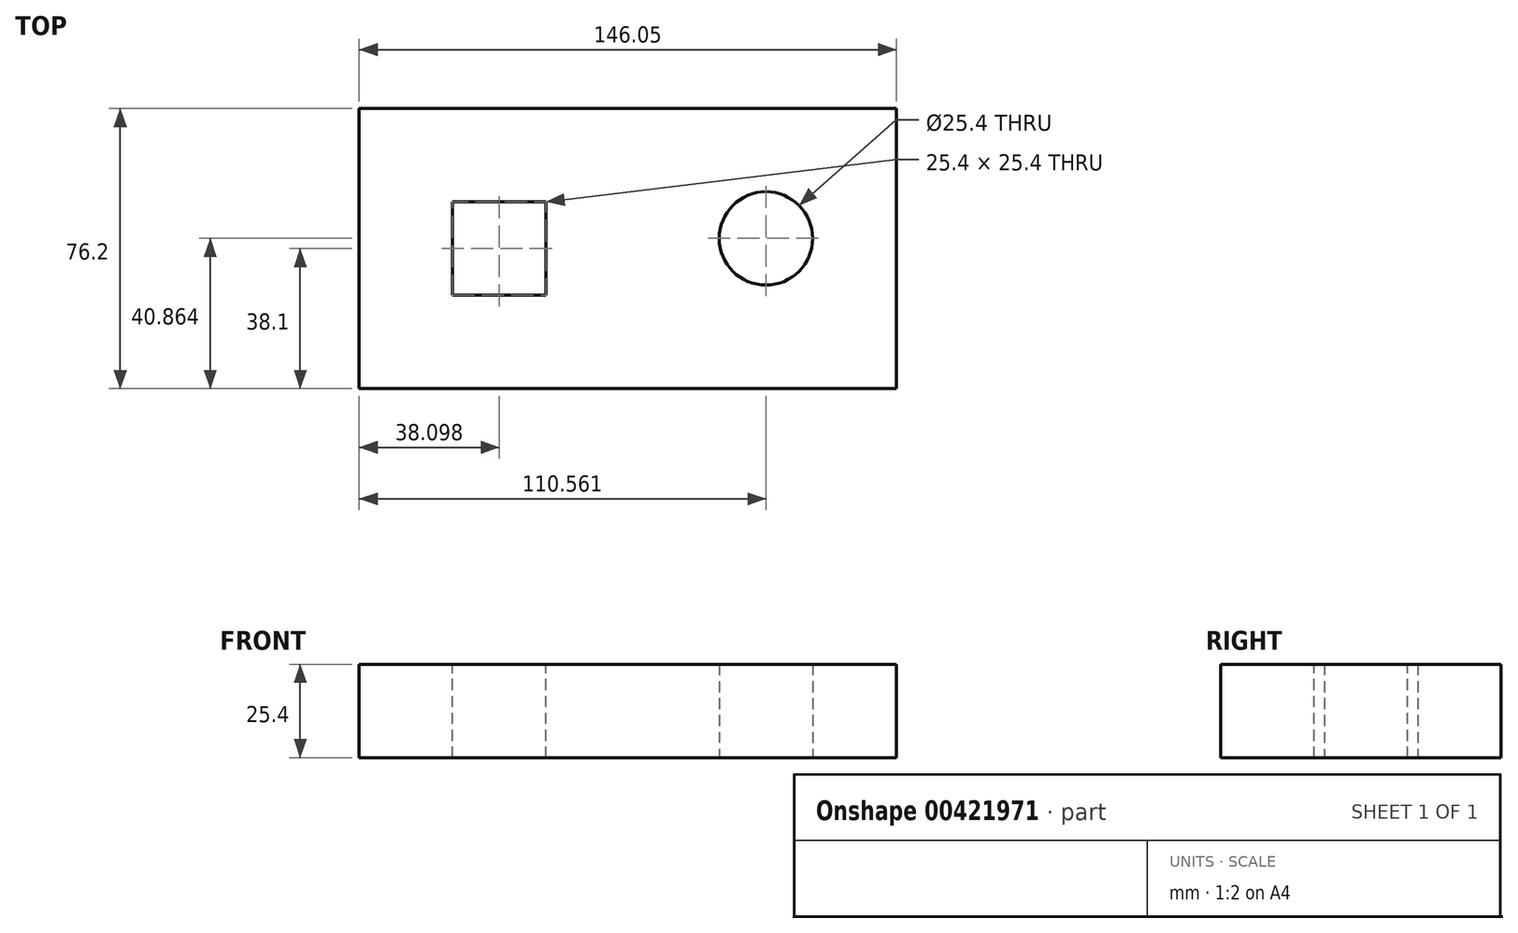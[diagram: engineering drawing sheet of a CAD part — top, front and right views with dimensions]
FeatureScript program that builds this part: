
annotation { "Feature Type Name" : "Feature", "Feature Type Description" : "" }
export const myFeature = defineFeature(function(context is Context, id is Id, definition is map)
    precondition{}
    {
        {
            var Q0;
            Q0=qCreatedBy(makeId("Top.planeOp"),FACE);
            var sketch = newSketch(context, id + "F0", { "sketchPlane" : qUnion([Q0])});
            skLineSegment(sketch, "E0.bottom", {"start": v(-76.38, 0) * mm, "end": v(69.67, 0) * mm});
            skLineSegment(sketch, "E0.top", {"start": v(-76.38, 76.2) * mm, "end": v(69.67, 76.2) * mm});
            skLineSegment(sketch, "E0.left", {"start": v(-76.38, 0) * mm, "end": v(-76.38, 76.2) * mm});
            skLineSegment(sketch, "E0.right", {"start": v(69.67, 0) * mm, "end": v(69.67, 76.2) * mm});
            skSolve(sketch);
        }
        {
            var Q0;
            Q0=makeQuery(id+"F0.imprint","IMPRINT",FACE,{"disambiguationData":[TD([[makeQuery(id+"F0.imprint","IMPRINT",EDGE,{"derivedFrom":sQuery(id+"F0.wireOp",EDGE,"E0.bottom")}),1.0]])]});
            var sketch = newSketch(context, id + "F1", { "sketchPlane" : qUnion([Q0])});
            skCircle(sketch, "E1", {"center": v(34.18, 40.86) * mm, "radius": 12.7 * mm});
            skSolve(sketch);
        }
        {
            var Q0;
            Q0=makeQuery(id+"F1.imprint","IMPRINT",FACE,{"disambiguationData":[TD([[makeQuery(id+"F1.imprint","IMPRINT",EDGE,{"derivedFrom":sQuery(id+"F1.wireOp",EDGE,"E1")}),-1.0]])]});
            extrude(context, id + "F2", {"entities" : qUnion([Q0]), "depth" : 25.4 * mm});
        }
        {
            var Q0;
            Q0=makeQuery(id+"F2.opExtrude","CAP_FACE",FACE,{"disambiguationData":[OSD([sQuery(id+"F0.wireOp",EDGE,"E0.bottom"),sQuery(id+"F0.wireOp",EDGE,"E0.top"),sQuery(id+"F0.wireOp",EDGE,"E0.left"),sQuery(id+"F0.wireOp",EDGE,"E0.right"),sQuery(id+"F1.wireOp",EDGE,"E1")])],"isStart":false});
            var sketch = newSketch(context, id + "F3", { "sketchPlane" : qUnion([Q0])});
            skLineSegment(sketch, "E2.bottom", {"start": v(-50.98, 50.8) * mm, "end": v(-25.58, 50.8) * mm});
            skLineSegment(sketch, "E2.top", {"start": v(-50.98, 25.4) * mm, "end": v(-25.58, 25.4) * mm});
            skLineSegment(sketch, "E2.left", {"start": v(-50.98, 50.8) * mm, "end": v(-50.98, 25.4) * mm});
            skLineSegment(sketch, "E2.right", {"start": v(-25.58, 50.8) * mm, "end": v(-25.58, 25.4) * mm});
            skSolve(sketch);
        }
        {
            var Q0;
            Q0=makeQuery(id+"F3.imprint","IMPRINT",FACE,{"disambiguationData":[TD([[makeQuery(id+"F3.imprint","IMPRINT",EDGE,{"derivedFrom":sQuery(id+"F3.wireOp",EDGE,"E2.bottom")}),-1.0]])]});
            extrude(context, id + "F4", {"entities" : qUnion([Q0]), "operationType" : NewBodyOperationType.REMOVE, "oppositeDirection" : true, "depth" : 25.4 * mm});
        }
    });
